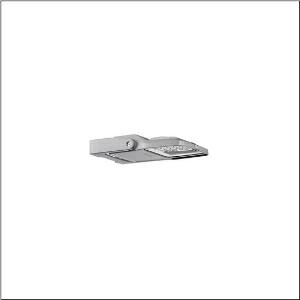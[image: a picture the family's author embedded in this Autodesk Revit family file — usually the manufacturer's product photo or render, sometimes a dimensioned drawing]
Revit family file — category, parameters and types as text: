
# Revit family: floodlight_fl_21_iq_micro___pl52_5xa7761a4d2a_29c7
name_source: partatom
category: Lighting Fixtures
units: mm (PartAtom-declared; Revit-internal decimal feet)

## family parameters
Cut with Voids When Loaded = No
Host = Face
Light Source = No
Part Type = Normal
Room Calculation Point = No
Round Connector Dimension = Use Diameter
Shared = No

## types (1)
- --- (1 x LED, 3010 lm, 23.1 W, 4000K)
    Apparent Load = 23 VA
    CIE Flux Codes = 26 60 98 100 100
    Color Rendering = 70
    Color Temperature = 4000K
    Default Elevation = 1800 mm
    Description = Floodlight FL 21 iQ micro, floodlight, primary light control with lens, of PMMA, primary optical cover: protective disc, of toughened safety glass, transparent, light distribution: PL52, light emission: direct distribution, installation type: surface-mounted, LED, High Power LED, rated luminous flux: 3.010lm, luminous efficacy: 130lm/W, light colour: 740, colour temperature: 4000K, control: optimised constant luminous flux control (CLO 2.0), Desk-Remote (wireless, voltage-free reading and setting of iQ features in the workshop via application-optimized NFC function/RFID function), Light-Fading, Smart-Wire, Night-Set, Lumen-Switch, Temp-Guard, Auto-Match, with terminal, 6-pole, mains connection: 220..240V, AC, 50/60Hz, start of lifetime: 23W, end of service life: 24W, reduction: 11W, luminaire housing, of diecast aluminium, powder-coated, Siteco® metallic grey (DB 702S), corrosivity category C5 mid according to DIN EN ISO 12944, sealing non-destructively replaceable, design bracket, of diecast aluminium, powder-coated, Siteco® metallic grey (DB 702S), protection rating (complete): IP66, insulation class (complete): insulation class II (safety insulation), certification: CE, ENEC, VDE, protection symbol: D, impact resistance: IK07, permissible operating ambient temperature: -40..+40°C, permissible operating ambient temperature for outdoor applications: -40..+50°C, standard: DIN EN 12944, LABS conformity tested according to VDMA 24364:2018-05, packaging unit: 1 piece

Light Distribution: PL52
    Height = 65 mm
    Lamp = 1 x LED
    Lamp Light Flux = 3010 lm
    Lamp Power = 23.1 W
    Lamp count = 1
    Length = 312 mm
    Luminous efficacy = 130 lm/W
    Manufacturer = Siteco
    ModVariant = No
    Model = 5XA7761A4D2A
    Mounting Place = Wall
    Mounting Type = Surface mounted
    Number of Poles = 1
    OnlyDefault = Yes
    Power Factor = 1
    Product Name = Floodlight FL 21 iQ micro | PL52
    Product group = floodlight | wall mounted
    ProductGroupID = 2001
    Protection Class = Protection class II
    Protection Degree = IP 66
    RLX_Detail_Level = 1
    RLX_Emergency_Light_Flux = 0 lm
    RLX_Emergency_Type = 0
    RLX_Emergency_Type_DB = No
    RlxData = <blob elided: 97553 chars, md5=ccea61f0>
    Socket = socket
    Standby Power = 0 W
    System Light Flux = 3010 lm
    System Power = 23 W
    Type Comments = factory setting: luminous flux: 100 % | dim-lin: 254 | 455 mA
    Type Image = l_1006878.jpg
    URL = http://relux.com
    VarID = @adj_149311
    Voltage = 0 V
    Weight = 0.00 kg
    Width = 230 mm

## geometry (parser evidence)
native form markers: Blend x4, Sweep x13
no freeform markers — native parametric forms only
